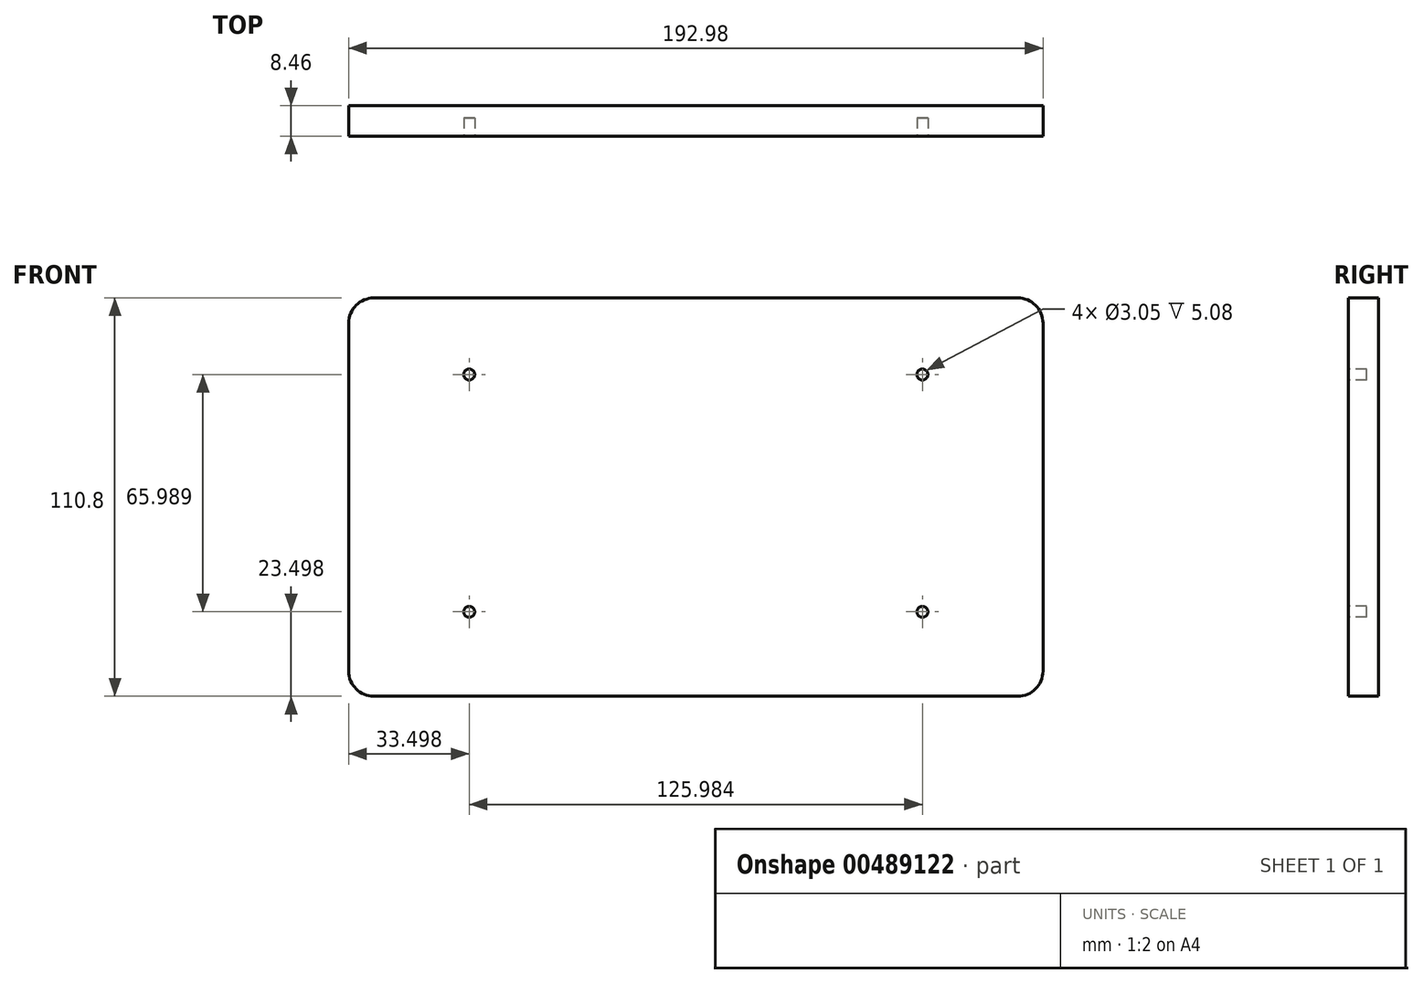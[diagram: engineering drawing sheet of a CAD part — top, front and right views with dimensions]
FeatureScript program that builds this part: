
annotation { "Feature Type Name" : "Feature", "Feature Type Description" : "" }
export const myFeature = defineFeature(function(context is Context, id is Id, definition is map)
    precondition{}
    {
        {
            var Q0;
            Q0=qCreatedBy(makeId("Front.planeOp"),FACE);
            var sketch = newSketch(context, id + "F0", { "sketchPlane" : qUnion([Q0])});
            skLineSegment(sketch, "E0.bottom", {"start": v(89.48, 55.4) * mm, "end": v(-89.48, 55.4) * mm});
            skLineSegment(sketch, "E0.top", {"start": v(89.48, -55.4) * mm, "end": v(-89.48, -55.4) * mm});
            skLineSegment(sketch, "E0.left", {"start": v(96.5, 48.39) * mm, "end": v(96.5, -48.39) * mm});
            skLineSegment(sketch, "E0.right", {"start": v(-96.5, 48.39) * mm, "end": v(-96.5, -48.39) * mm});
            skPoint(sketch, "E0.middle", {"position": v(0, 0) * mm});
            skPoint(sketch, "E1.visualSharp", {"position": v(-96.5, 55.4) * mm});
            skArc(sketch, "E1.filletArc", {"start": v(-89.48, 55.4) * mm, "mid": v(-94.44, 53.34) * mm, "end": v(-96.5, 48.39) * mm});
            skPoint(sketch, "E2.visualSharp", {"position": v(-96.5, -55.4) * mm});
            skArc(sketch, "E2.filletArc", {"start": v(-96.5, -48.39) * mm, "mid": v(-94.44, -53.34) * mm, "end": v(-89.48, -55.4) * mm});
            skPoint(sketch, "E3.visualSharp", {"position": v(96.5, -55.4) * mm});
            skArc(sketch, "E3.filletArc", {"start": v(89.48, -55.4) * mm, "mid": v(94.44, -53.34) * mm, "end": v(96.5, -48.39) * mm});
            skPoint(sketch, "E4.visualSharp", {"position": v(96.5, 55.4) * mm});
            skArc(sketch, "E4.filletArc", {"start": v(96.5, 48.39) * mm, "mid": v(94.44, 53.34) * mm, "end": v(89.48, 55.4) * mm});
            skSolve(sketch);
        }
        {
            var Q0;
            Q0=makeQuery(id+"F0.imprint","IMPRINT",FACE,{"disambiguationData":[TD([[makeQuery(id+"F0.imprint","IMPRINT",EDGE,{"derivedFrom":sQuery(id+"F0.wireOp",EDGE,"E0.bottom")}),1.0]])]});
            extrude(context, id + "F1", {"entities" : qUnion([Q0]), "depth" : 8.46 * mm});
        }
        {
            var Q0;
            Q0=makeQuery(id+"F1.opExtrude","CAP_FACE",FACE,{"disambiguationData":[OSD([sQuery(id+"F0.wireOp",EDGE,"E0.bottom"),sQuery(id+"F0.wireOp",EDGE,"E0.top"),sQuery(id+"F0.wireOp",EDGE,"E0.left"),sQuery(id+"F0.wireOp",EDGE,"E0.right"),sQuery(id+"F0.wireOp",EDGE,"E1.filletArc"),sQuery(id+"F0.wireOp",EDGE,"E2.filletArc"),sQuery(id+"F0.wireOp",EDGE,"E3.filletArc"),sQuery(id+"F0.wireOp",EDGE,"E4.filletArc")])],"isStart":false});
            var sketch = newSketch(context, id + "F2", { "sketchPlane" : qUnion([Q0])});
            skCircle(sketch, "E5", {"center": v(-63, 34.09) * mm, "radius": 1.52 * mm});
            skCircle(sketch, "E6", {"center": v(63, 34.09) * mm, "radius": 1.52 * mm});
            skCircle(sketch, "E7", {"center": v(63, -31.9) * mm, "radius": 1.52 * mm});
            skCircle(sketch, "E8", {"center": v(-63, -31.9) * mm, "radius": 1.52 * mm});
            skSolve(sketch);
        }
        {
            var Q0;
            Q0=makeQuery(id+"F2.imprint","IMPRINT",FACE,{"disambiguationData":[TD([[makeQuery(id+"F2.imprint","IMPRINT",EDGE,{"derivedFrom":sQuery(id+"F2.wireOp",EDGE,"E5")}),1.0]])]});
            var Q1;
            Q1=makeQuery(id+"F2.imprint","IMPRINT",FACE,{"disambiguationData":[TD([[makeQuery(id+"F2.imprint","IMPRINT",EDGE,{"derivedFrom":sQuery(id+"F2.wireOp",EDGE,"E6")}),1.0]])]});
            var Q2;
            Q2=makeQuery(id+"F2.imprint","IMPRINT",FACE,{"disambiguationData":[TD([[makeQuery(id+"F2.imprint","IMPRINT",EDGE,{"derivedFrom":sQuery(id+"F2.wireOp",EDGE,"E7")}),1.0]])]});
            var Q3;
            Q3=makeQuery(id+"F2.imprint","IMPRINT",FACE,{"disambiguationData":[TD([[makeQuery(id+"F2.imprint","IMPRINT",EDGE,{"derivedFrom":sQuery(id+"F2.wireOp",EDGE,"E8")}),1.0]])]});
            extrude(context, id + "F3", {"entities" : qUnion([Q0, Q1, Q2, Q3]), "operationType" : NewBodyOperationType.REMOVE, "oppositeDirection" : true, "depth" : 5.08 * mm});
        }
    });
